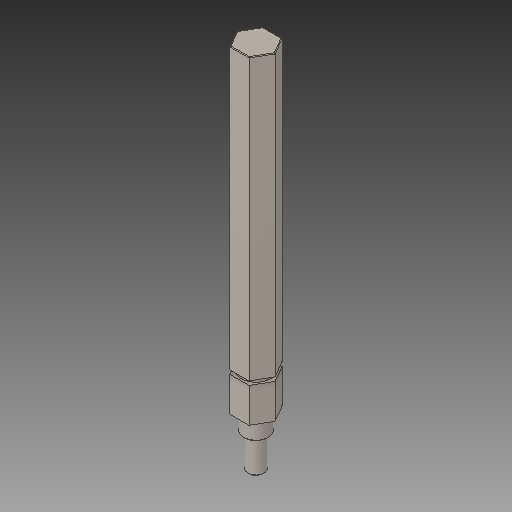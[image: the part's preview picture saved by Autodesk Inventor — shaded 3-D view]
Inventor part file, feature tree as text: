
AUTODESK INVENTOR PART (.ipt)
format: ipt  version: 2018.2 (Build 222227000, 227)  size: 98,816 bytes
history: native  units: in
note: dims shown in document units (in); Inventor stores cm internally (conversion verified against a paired STEP export)
features: chamfer x1
ambient origin geometry x8: Origin, YZ Plane, XZ Plane, XY Plane, X Axis, Y Axis, Z Axis, Center Point
bodies: Solid1 (feature_tree)
feature tree (1):
  chamfer  "Chamfer1"  [1 undecoded]
note: 1 required parameter value undecoded (feature->parameter linkage not recoverable at this tier; creation-order binding heuristic only, values carry confidence <= 0.55)
